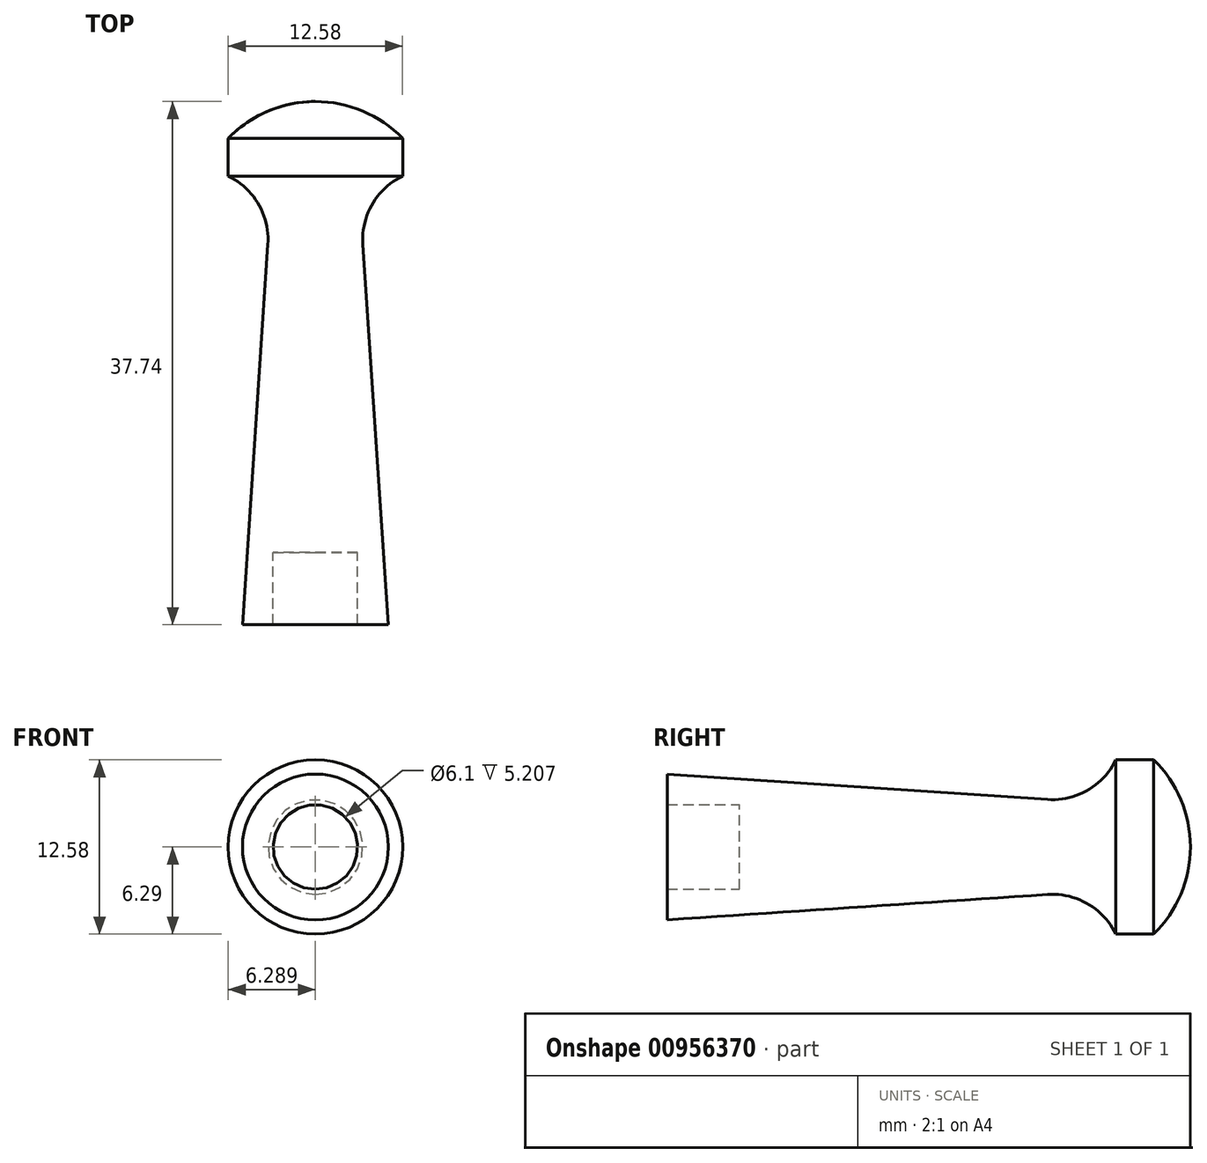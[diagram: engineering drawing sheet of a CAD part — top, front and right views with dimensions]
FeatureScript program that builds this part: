
annotation { "Feature Type Name" : "Feature", "Feature Type Description" : "" }
export const myFeature = defineFeature(function(context is Context, id is Id, definition is map)
    precondition{}
    {
        {
            var Q0;
            Q0=qCreatedBy(makeId("Top.planeOp"),FACE);
            var sketch = newSketch(context, id + "F0", { "sketchPlane" : qUnion([Q0])});
            skLineSegment(sketch, "E0", {"start": v(0, 0) * mm, "end": v(0, -2.94) * mm, "construction": true});
            skLineSegment(sketch, "E1", {"start": v(49.57, 43.6) * mm, "end": v(52.62, 43.58) * mm});
            skLineSegment(sketch, "E2", {"start": v(52.62, 43.58) * mm, "end": v(52.62, 86.4) * mm});
            skLineSegment(sketch, "E3", {"start": v(49.57, 43.6) * mm, "end": v(49.57, 48.66) * mm});
            skLineSegment(sketch, "E4", {"start": v(49.57, 48.66) * mm, "end": v(47.36, 48.66) * mm});
            skLineSegment(sketch, "E5", {"start": v(47.36, 48.66) * mm, "end": v(49.2, 76.1) * mm});
            skArc(sketch, "E6", {"start": v(49.2, 76.1) * mm, "mid": v(48.51, 79) * mm, "end": v(46.33, 81.02) * mm});
            skLineSegment(sketch, "E7", {"start": v(46.33, 81.02) * mm, "end": v(46.33, 83.75) * mm});
            skLineSegment(sketch, "E8", {"start": v(46.33, 83.75) * mm, "end": v(52.62, 86.4) * mm, "construction": true});
            skLineSegment(sketch, "E9.MirrorCS", {"start": v(58.91, 83.75) * mm, "end": v(52.62, 86.4) * mm, "construction": true});
            skArc(sketch, "E10", {"start": v(52.62, 86.4) * mm, "mid": v(49.2, 85.71) * mm, "end": v(46.33, 83.75) * mm});
            skPoint(sketch, "E11.MirrorCS.end.orphan", {"position": v(58.91, 83.75) * mm});
            skPoint(sketch, "E11.MirrorCS.start.orphan", {"position": v(58.91, 81.02) * mm});
            skPoint(sketch, "E12.MirrorCS.start.orphan", {"position": v(56.04, 76.1) * mm});
            skPoint(sketch, "E13.MirrorCS.start.orphan", {"position": v(57.88, 48.66) * mm});
            skPoint(sketch, "E14.MirrorCS.start.orphan", {"position": v(55.67, 48.66) * mm});
            skPoint(sketch, "E15.MirrorCS.start.orphan", {"position": v(55.67, 43.6) * mm});
            skPoint(sketch, "E16.MirrorCS.end.orphan", {"position": v(52.62, 43.58) * mm});
            skSolve(sketch);
        }
        {
            var Q0;
            Q0=makeQuery(id+"F0.imprint","IMPRINT",FACE,{"disambiguationData":[TD([[makeQuery(id+"F0.imprint","IMPRINT",EDGE,{"derivedFrom":sQuery(id+"F0.wireOp",EDGE,"E1")}),1.0]])]});
            var Q1;
            Q1 = qConstructionFilter(qBodyType(qCreatedBy(id + "F0" ,EDGE), BodyType.WIRE), ConstructionObject.NO);
            var Q2;
            Q2=sQuery(id+"F0.wireOp",EDGE,"E2");
            revolve(context, id + "F1", {"surfaceOperationType" : NewSurfaceOperationType.NEW, "entities" : qUnion([Q0]), "surfaceEntities" : qUnion([Q1]), "axis" : qUnion([Q2]), "revolveType" : RevolveType.FULL});
        }
        {
            var Q0;
            Q0=makeQuery(id+"F1.opRevolve","SWEPT_FACE",FACE,{"disambiguationData":[OSD([sQuery(id+"F0.wireOp",EDGE,"E4")])]});
            var sketch = newSketch(context, id + "F2", { "sketchPlane" : qUnion([Q0])});
            skCircle(sketch, "E17", {"center": v(52.62, 0) * mm, "radius": 3.05 * mm});
            skSolve(sketch);
        }
        {
            var Q0;
            Q0 = qSketchRegion(id + "F2", true);
            extrude(context, id + "F3", {"entities" : qUnion([Q0]), "operationType" : NewBodyOperationType.REMOVE, "endBound" : BoundingType.SYMMETRIC, "depth" : 10.4 * mm, "offsetDistance" : 25.4 * mm});
        }
    });
